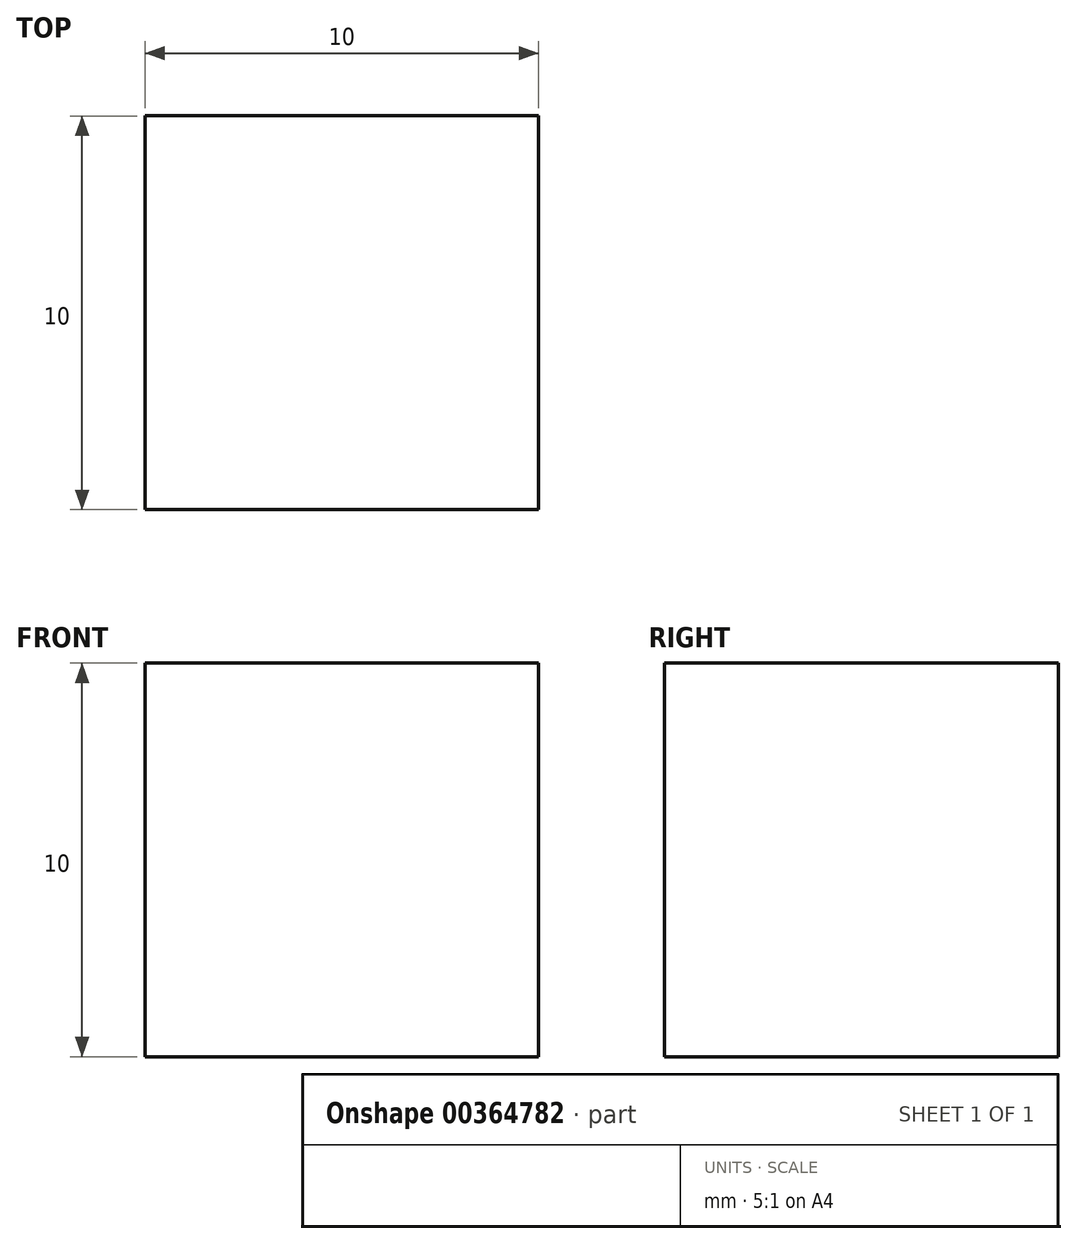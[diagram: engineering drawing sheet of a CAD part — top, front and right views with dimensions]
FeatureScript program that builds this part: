
annotation { "Feature Type Name" : "Feature", "Feature Type Description" : "" }
export const myFeature = defineFeature(function(context is Context, id is Id, definition is map)
    precondition{}
    {
        {
            var Q0;
            Q0=qCreatedBy(makeId("Top.planeOp"),FACE);
            var sketch = newSketch(context, id + "F0", { "sketchPlane" : qUnion([Q0])});
            skLineSegment(sketch, "E0.bottom", {"start": v(-36.53, 32.95) * mm, "end": v(-26.53, 32.95) * mm});
            skLineSegment(sketch, "E0.top", {"start": v(-36.53, 22.95) * mm, "end": v(-26.53, 22.95) * mm});
            skLineSegment(sketch, "E0.left", {"start": v(-36.53, 32.95) * mm, "end": v(-36.53, 22.95) * mm});
            skLineSegment(sketch, "E0.right", {"start": v(-26.53, 32.95) * mm, "end": v(-26.53, 22.95) * mm});
            skSolve(sketch);
        }
        {
            var Q0;
            Q0=makeQuery(id+"F0.imprint","IMPRINT",FACE,{"disambiguationData":[TD([[makeQuery(id+"F0.imprint","IMPRINT",EDGE,{"derivedFrom":sQuery(id+"F0.wireOp",EDGE,"E0.bottom")}),-1.0]])]});
            extrude(context, id + "F1", {"entities" : qUnion([Q0]), "depth" : 10 * mm});
        }
    });
